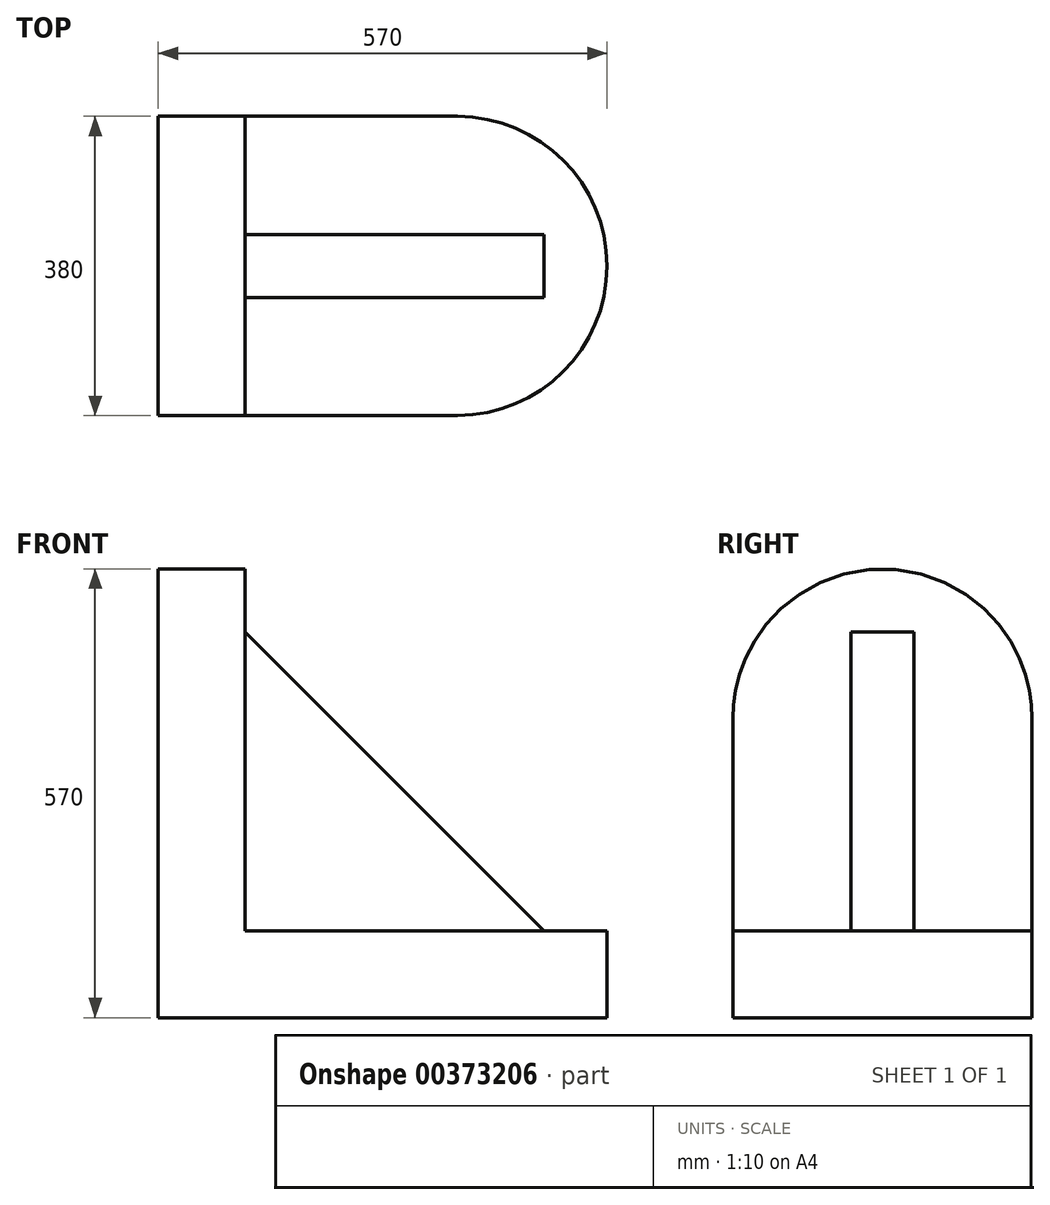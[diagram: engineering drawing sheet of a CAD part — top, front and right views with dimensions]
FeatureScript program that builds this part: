
annotation { "Feature Type Name" : "Feature", "Feature Type Description" : "" }
export const myFeature = defineFeature(function(context is Context, id is Id, definition is map)
    precondition{}
    {
        {
            var Q0;
            Q0=qCreatedBy(makeId("Top.planeOp"),FACE);
            var sketch = newSketch(context, id + "F0", { "sketchPlane" : qUnion([Q0])});
            skLineSegment(sketch, "E0.bottom", {"start": v(190, 190) * mm, "end": v(-190, 190) * mm});
            skLineSegment(sketch, "E0.top", {"start": v(190, -190) * mm, "end": v(-190, -190) * mm});
            skLineSegment(sketch, "E0.left", {"start": v(190, 190) * mm, "end": v(190, -190) * mm});
            skLineSegment(sketch, "E0.right", {"start": v(-190, 190) * mm, "end": v(-190, -190) * mm});
            skPoint(sketch, "E0.middle", {"position": v(0, 0) * mm});
            skCircle(sketch, "E1", {"center": v(190, 0) * mm, "radius": 190 * mm});
            skSolve(sketch);
        }
        {
            var Q0;
            {var subQ0=sQuery(id+"F0.wireOp",EDGE,"E0.bottom");Q0=makeQuery(id+"F0.imprint","IMPRINT",FACE,{"disambiguationData":[TD([[makeQuery(id+"F0.imprint","IMPRINT",EDGE,{"derivedFrom":subQ0}),1.0]])]});}
            var Q1;
            {var subQ0=sQuery(id+"F0.wireOp",EDGE,"E0.left");Q1=makeQuery(id+"F0.imprint","IMPRINT",FACE,{"disambiguationData":[TD([[makeQuery(id+"F0.imprint","IMPRINT",EDGE,{"derivedFrom":subQ0}),1.0]])]});}
            var Q2;
            {var subQ0=sQuery(id+"F0.wireOp",EDGE,"E0.left");Q2=makeQuery(id+"F0.imprint","IMPRINT",FACE,{"disambiguationData":[TD([[makeQuery(id+"F0.imprint","IMPRINT",EDGE,{"derivedFrom":subQ0}),-1.0]])]});}
            extrude(context, id + "F1", {"entities" : qUnion([Q0, Q1, Q2]), "depth" : 110 * mm});
        }
        {
            var Q0;
            Q0=makeQuery(id+"F1.opExtrude","CAP_FACE",FACE,{"disambiguationData":[OSD([sQuery(id+"F0.wireOp",EDGE,"E0.bottom"),sQuery(id+"F0.wireOp",EDGE,"E0.top"),sQuery(id+"F0.wireOp",EDGE,"E0.right"),sQuery(id+"F0.wireOp",EDGE,"E1")])],"isStart":false});
            var sketch = newSketch(context, id + "F2", { "sketchPlane" : qUnion([Q0])});
            skLineSegment(sketch, "E2.bottom", {"start": v(-190, 190) * mm, "end": v(-80, 190) * mm});
            skLineSegment(sketch, "E2.top", {"start": v(-190, -190) * mm, "end": v(-80, -190) * mm});
            skLineSegment(sketch, "E2.left", {"start": v(-190, 190) * mm, "end": v(-190, -190) * mm});
            skLineSegment(sketch, "E2.right", {"start": v(-80, 190) * mm, "end": v(-80, -190) * mm});
            skSolve(sketch);
        }
        {
            var Q0;
            Q0=makeQuery(id+"F2.imprint","IMPRINT",FACE,{"disambiguationData":[TD([[makeQuery(id+"F2.imprint","IMPRINT",EDGE,{"derivedFrom":sQuery(id+"F2.wireOp",EDGE,"E2.bottom")}),1.0]])]});
            extrude(context, id + "F3", {"entities" : qUnion([Q0]), "operationType" : NewBodyOperationType.ADD, "depth" : 270 * mm});
        }
        {
            var Q0;
            Q0=makeQuery(id+"F3.boolean.opBoolean","MERGE",FACE,{"derivedFrom":[makeQuery(id+"F1.opExtrude","SWEPT_FACE",FACE,{"disambiguationData":[OSD([sQuery(id+"F0.wireOp",EDGE,"E0.right")])]}),makeQuery(id+"F3.opExtrude","SWEPT_FACE",FACE,{"disambiguationData":[OSD([sQuery(id+"F2.wireOp",EDGE,"E2.left")])]})]});
            var sketch = newSketch(context, id + "F4", { "sketchPlane" : qUnion([Q0])});
            skPoint(sketch, "E3.endSnap0", {"position": v(0, 380) * mm});
            skPoint(sketch, "E4", {"position": v(0, 190) * mm});
            skArc(sketch, "E5", {"start": v(190, 380) * mm, "mid": v(0, 570) * mm, "end": v(-190, 380) * mm});
            skPoint(sketch, "E5.first.point", {"position": v(-190, 380) * mm});
            skPoint(sketch, "E5.second.point", {"position": v(190, 380) * mm});
            skSolve(sketch);
        }
        {
            var Q0;
            Q0=makeQuery(id+"F4.imprint","IMPRINT",FACE,{"disambiguationData":[TD([[makeQuery(id+"F4.imprint","IMPRINT",EDGE,{"derivedFrom":sQuery(id+"F4.wireOp",EDGE,"E5")}),1.0]])]});
            extrude(context, id + "F5", {"entities" : qUnion([Q0]), "operationType" : NewBodyOperationType.ADD, "oppositeDirection" : true, "depth" : 110 * mm});
        }
        {
            var Q0;
            Q0=makeQuery(id+"F1.opExtrude","CAP_FACE",FACE,{"disambiguationData":[OSD([sQuery(id+"F0.wireOp",EDGE,"E0.bottom"),sQuery(id+"F0.wireOp",EDGE,"E0.top"),sQuery(id+"F0.wireOp",EDGE,"E0.right"),sQuery(id+"F0.wireOp",EDGE,"E1")])],"isStart":false});
            var sketch = newSketch(context, id + "F6", { "sketchPlane" : qUnion([Q0])});
            skLineSegment(sketch, "E6", {"start": v(-80, -40) * mm, "end": v(300, -40) * mm});
            skLineSegment(sketch, "E7", {"start": v(300, -40) * mm, "end": v(300, 40) * mm});
            skLineSegment(sketch, "E8", {"start": v(300, 40) * mm, "end": v(-80, 40) * mm});
            skLineSegment(sketch, "E9", {"start": v(-80, -190) * mm, "end": v(-80, -40) * mm});
            skLineSegment(sketch, "E10", {"start": v(-80, 40) * mm, "end": v(-80, 190) * mm});
            skLineSegment(sketch, "E11", {"start": v(-80, 190) * mm, "end": v(-80, 40) * mm});
            skSolve(sketch);
        }
        {
            var Q0;
            {var subQ0=sQuery(id+"F6.wireOp",EDGE,"E6");Q0=makeQuery(id+"F6.imprint","IMPRINT",FACE,{"disambiguationData":[TD([[makeQuery(id+"F6.imprint","IMPRINT",EDGE,{"derivedFrom":subQ0}),1.0]])]});}
            extrude(context, id + "F7", {"entities" : qUnion([Q0]), "operationType" : NewBodyOperationType.ADD, "depth" : 380 * mm});
        }
        {
            var Q0;
            Q0=makeQuery(id+"F7.opExtrude","SWEPT_FACE",FACE,{"disambiguationData":[OSD([sQuery(id+"F6.wireOp",EDGE,"E6")])]});
            var sketch = newSketch(context, id + "F8", { "sketchPlane" : qUnion([Q0])});
            skLineSegment(sketch, "E12", {"start": v(-80, 490) * mm, "end": v(300, 110) * mm});
            skLineSegment(sketch, "E13", {"start": v(300, 110) * mm, "end": v(300, 490) * mm});
            skLineSegment(sketch, "E14", {"start": v(300, 490) * mm, "end": v(-80, 490) * mm});
            skSolve(sketch);
        }
        {
            var Q0;
            Q0=makeQuery(id+"F8.imprint","IMPRINT",FACE,{"disambiguationData":[TD([[makeQuery(id+"F8.imprint","IMPRINT",EDGE,{"derivedFrom":sQuery(id+"F8.wireOp",EDGE,"E12")}),1.0]])]});
            extrude(context, id + "F9", {"entities" : qUnion([Q0]), "operationType" : NewBodyOperationType.REMOVE, "endBound" : BoundingType.UP_TO_NEXT, "oppositeDirection" : true, "depth" : 25 * mm});
        }
    });
